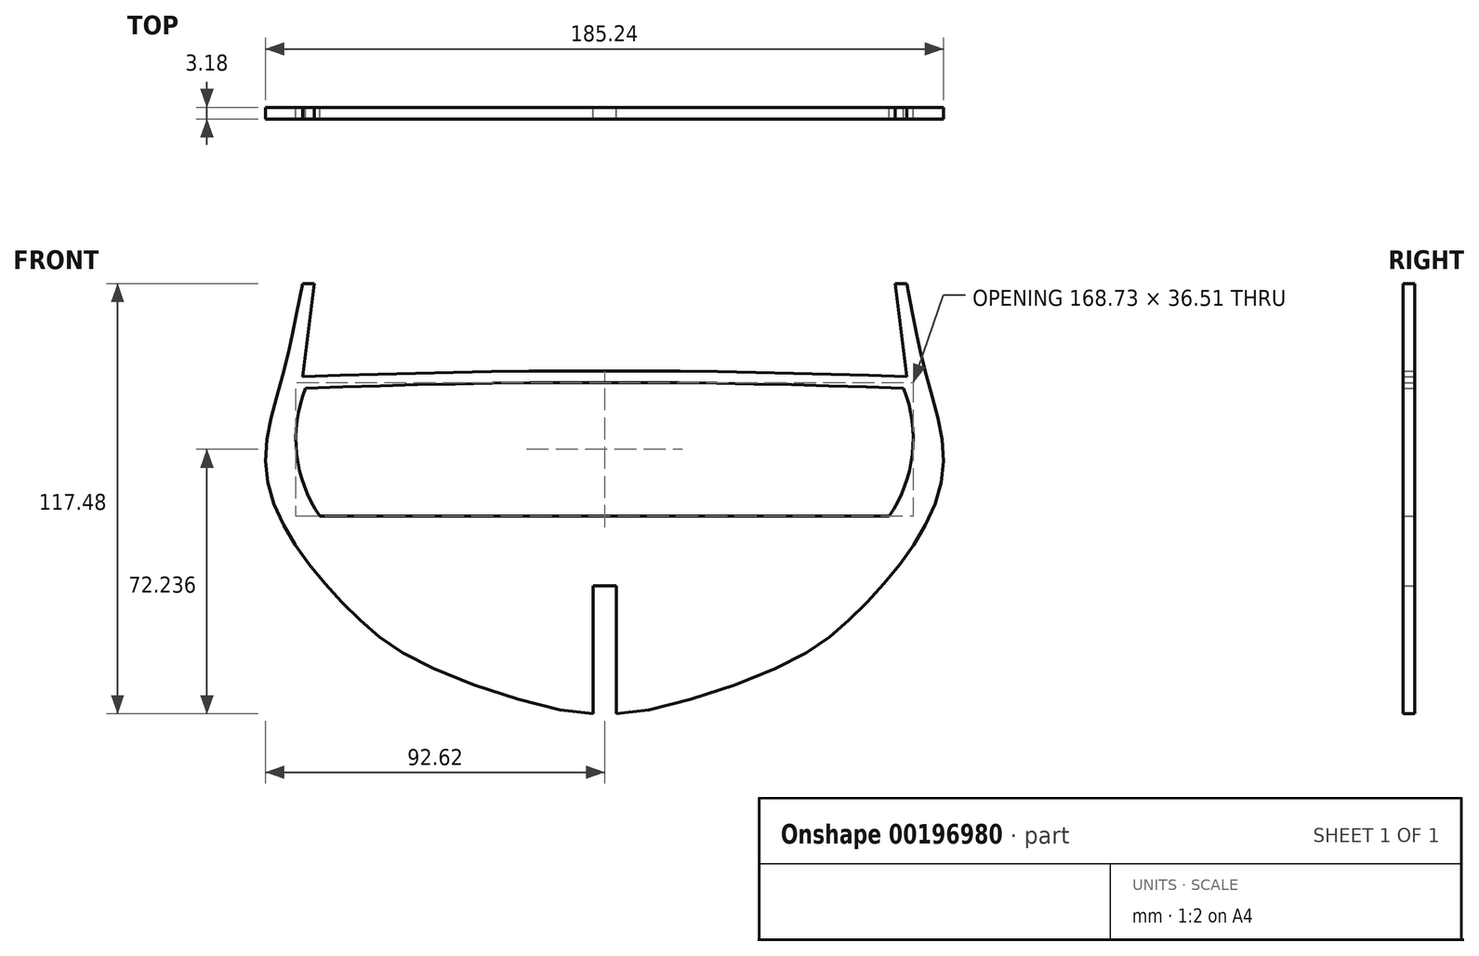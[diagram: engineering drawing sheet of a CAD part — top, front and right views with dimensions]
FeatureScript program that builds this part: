
annotation { "Feature Type Name" : "Feature", "Feature Type Description" : "" }
export const myFeature = defineFeature(function(context is Context, id is Id, definition is map)
    precondition{}
    {
        {
            var Q0;
            Q0=qCreatedBy(makeId("Front.planeOp"),FACE);
            var sketch = newSketch(context, id + "F0", { "sketchPlane" : qUnion([Q0])});
            skLineSegment(sketch, "E0", {"start": v(0, 0) * mm, "end": v(0, -53.97) * mm, "construction": true});
            skLineSegment(sketch, "E1", {"start": v(0, 0) * mm, "end": v(0, 34.93) * mm, "construction": true});
            skLineSegment(sketch, "E2", {"start": v(0, 34.93) * mm, "end": v(-81.76, 34.93) * mm, "construction": true});
            skLineSegment(sketch, "E3", {"start": v(0, 34.93) * mm, "end": v(81.76, 34.93) * mm, "construction": true});
            skLineSegment(sketch, "E4", {"start": v(81.76, 34.93) * mm, "end": v(88.9, 34.93) * mm, "construction": true});
            skLineSegment(sketch, "E5", {"start": v(0, 0) * mm, "end": v(77.79, 0) * mm});
            skLineSegment(sketch, "E6", {"start": v(77.79, 0) * mm, "end": v(88.92, 0) * mm, "construction": true});
            skLineSegment(sketch, "E7", {"start": v(77.79, 0) * mm, "end": v(81.76, 34.93) * mm, "construction": true});
            skLineSegment(sketch, "E8", {"start": v(0, 0) * mm, "end": v(-77.79, 0) * mm});
            skLineSegment(sketch, "E9", {"start": v(-77.79, 0) * mm, "end": v(-81.76, 34.92) * mm, "construction": true});
            skLineSegment(sketch, "E10", {"start": v(-3.18, -53.98) * mm, "end": v(-3.18, -19.05) * mm});
            skLineSegment(sketch, "E11", {"start": v(-3.17, -19.05) * mm, "end": v(0, -19.05) * mm});
            skLineSegment(sketch, "E12", {"start": v(0, -19.05) * mm, "end": v(3.17, -19.05) * mm});
            skLineSegment(sketch, "E13", {"start": v(3.17, -19.05) * mm, "end": v(3.17, -53.98) * mm});
            skFitSpline(sketch, "E14", {"points": [v(3.18, -53.98) * mm, v(47.63, -41.27) * mm, v(66.68, -28.57) * mm, v(78.58, -15.88) * mm, v(87.31, -3.17) * mm, v(92.08, 9.52) * mm, v(92.08, 22.23) * mm, v(88.9, 34.93) * mm, v(85.73, 47.62) * mm, v(82.55, 63.5) * mm], "startDerivative": vector(165.75, 0) * mm, "endDerivative": vector(-45.2, 225.97) * mm});
            skArc(sketch, "E15", {"start": v(81.76, 34.93) * mm, "mid": v(0, 36.51) * mm, "end": v(-81.76, 34.93) * mm});
            skArc(sketch, "E16", {"start": v(82.55, 38.07) * mm, "mid": v(0, 39.69) * mm, "end": v(-82.55, 38.07) * mm});
            skLineSegment(sketch, "E17", {"start": v(3.17, -53.97) * mm, "end": v(-3.18, -53.97) * mm, "construction": true});
            skPoint(sketch, "E18", {"position": v(0, 36.51) * mm});
            skLineSegment(sketch, "E19", {"start": v(82.55, 38.07) * mm, "end": v(88.05, 38.07) * mm, "construction": true});
            skPoint(sketch, "E20", {"position": v(0, 39.69) * mm});
            skLineSegment(sketch, "E21", {"start": v(82.55, 38.07) * mm, "end": v(79.37, 63.5) * mm});
            skLineSegment(sketch, "E22", {"start": v(79.38, 63.5) * mm, "end": v(82.55, 63.5) * mm});
            skArc(sketch, "E23", {"start": v(-81.76, 34.92) * mm, "mid": v(-84.13, 16.97) * mm, "end": v(-77.79, 0) * mm});
            skArc(sketch, "E24", {"start": v(77.79, 0) * mm, "mid": v(84.13, 16.97) * mm, "end": v(81.76, 34.92) * mm});
            skLineSegment(sketch, "E25.MirrorCS", {"start": v(-82.55, 38.07) * mm, "end": v(-79.38, 63.5) * mm});
            skLineSegment(sketch, "E26.MirrorCS", {"start": v(-79.38, 63.5) * mm, "end": v(-82.55, 63.5) * mm});
            skFitSpline(sketch, "E27.MirrorCS", {"points": [v(-3.18, -53.98) * mm, v(-47.63, -41.27) * mm, v(-66.68, -28.57) * mm, v(-78.58, -15.88) * mm, v(-87.31, -3.17) * mm, v(-92.08, 9.52) * mm, v(-92.08, 22.23) * mm, v(-88.9, 34.93) * mm, v(-85.73, 47.62) * mm, v(-82.55, 63.5) * mm], "startDerivative": vector(-165.75, 0) * mm, "endDerivative": vector(45.2, 225.97) * mm});
            skSolve(sketch);
        }
        {
            var Q0;
            Q0=makeQuery(id+"F0.imprint","IMPRINT",FACE,{"disambiguationData":[TD([[makeQuery(id+"F0.imprint","IMPRINT",EDGE,{"derivedFrom":sQuery(id+"F0.wireOp",EDGE,"E5")}),-1.0]])]});
            extrude(context, id + "F1", {"entities" : qUnion([Q0]), "endBound" : BoundingType.SYMMETRIC, "depth" : 3.17 * mm});
        }
    });
